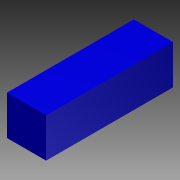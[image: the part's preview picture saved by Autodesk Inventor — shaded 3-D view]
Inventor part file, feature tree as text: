
AUTODESK INVENTOR PART (.ipt)
format: ipt  version: 2012 (Build 160160000, 160)  size: 70,144 bytes
history: native  units: in
note: dims shown in document units (in); Inventor stores cm internally (conversion verified against a paired STEP export)
features: extrude x1, sketch x1
ambient origin geometry x8: Origin, YZ Plane, XZ Plane, XY Plane, X Axis, Y Axis, Z Axis, Center Point
bodies: Solid1 (feature_tree)
feature tree (2):
  extrude  "Extrusion1"  Depth=1.3386in
  sketch  "Sketch1"  dims[d0=1.3386in d1=1.3386in d2=4.3307in d3=0.0in]
